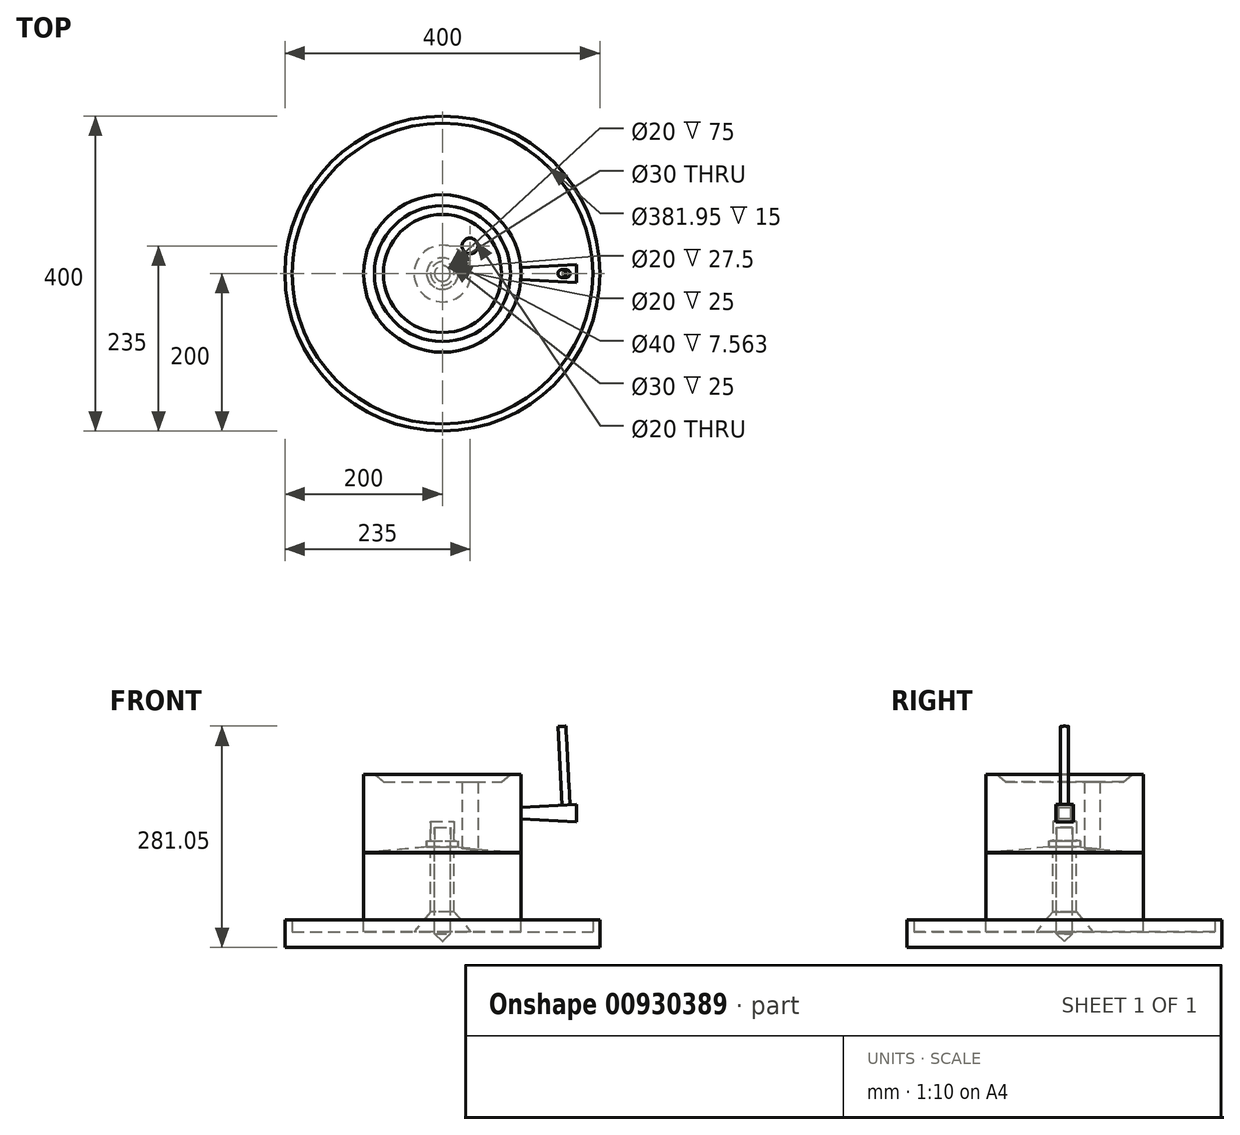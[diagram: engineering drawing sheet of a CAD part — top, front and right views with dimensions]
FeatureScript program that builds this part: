
annotation { "Feature Type Name" : "Feature", "Feature Type Description" : "" }
export const myFeature = defineFeature(function(context is Context, id is Id, definition is map)
    precondition{}
    {
        {
            var Q0;
            Q0=qCreatedBy(makeId("Top.planeOp"),FACE);
            var sketch = newSketch(context, id + "F0", { "sketchPlane" : qUnion([Q0])});
            skCircle(sketch, "E0", {"center": v(0, 0) * mm, "radius": 100 * mm});
            skCircle(sketch, "E1", {"center": v(35, 35) * mm, "radius": 10 * mm});
            skSolve(sketch);
        }
        {
            var Q0;
            Q0 = qSketchRegion(id + "F0", true);
            extrude(context, id + "F1", {"entities" : qUnion([Q0]), "depth" : 100 * mm, "offsetDistance" : 25 * mm});
        }
        {
            var Q0;
            Q0=qCreatedBy(makeId("Front.planeOp"),FACE);
            var sketch = newSketch(context, id + "F2", { "sketchPlane" : qUnion([Q0])});
            skLineSegment(sketch, "E2", {"start": v(0, 40) * mm, "end": v(15, 40) * mm});
            skLineSegment(sketch, "E3", {"start": v(0, 0) * mm, "end": v(0, 40) * mm});
            skLineSegment(sketch, "E4", {"start": v(15, 40) * mm, "end": v(15, 15) * mm});
            skLineSegment(sketch, "E5", {"start": v(15, 15) * mm, "end": v(20, 15) * mm});
            skLineSegment(sketch, "E6", {"start": v(20, 15) * mm, "end": v(20, 0) * mm});
            skLineSegment(sketch, "E7", {"start": v(0, 0) * mm, "end": v(20, 0) * mm});
            skSolve(sketch);
        }
        {
            var Q0;
            Q0 = qSketchRegion(id + "F2", true);
            var Q1;
            Q1=sQuery(id+"F2.wireOp",EDGE,"E3");
            revolve(context, id + "F3", {"operationType" : NewBodyOperationType.REMOVE, "surfaceOperationType" : NewSurfaceOperationType.NEW, "entities" : qUnion([Q0]), "axis" : qUnion([Q1]), "revolveType" : RevolveType.FULL, "oppositeDirection" : true});
        }
        {
            var Q0;
            Q0=qCreatedBy(makeId("Front.planeOp"),FACE);
            var sketch = newSketch(context, id + "F4", { "sketchPlane" : qUnion([Q0])});
            skLineSegment(sketch, "E8", {"start": v(0, 9.19) * mm, "end": v(105, 0) * mm});
            skLineSegment(sketch, "E9", {"start": v(105, 0) * mm, "end": v(0, 0) * mm});
            skLineSegment(sketch, "E10", {"start": v(0, 0) * mm, "end": v(0, 9.19) * mm});
            skSolve(sketch);
        }
        {
            var Q0;
            Q0 = qSketchRegion(id + "F4", true);
            var Q1;
            Q1=sQuery(id+"F4.wireOp",EDGE,"E10");
            revolve(context, id + "F5", {"operationType" : NewBodyOperationType.REMOVE, "surfaceOperationType" : NewSurfaceOperationType.NEW, "entities" : qUnion([Q0]), "axis" : qUnion([Q1]), "revolveType" : RevolveType.FULL, "oppositeDirection" : true});
        }
        {
            var Q0;
            Q0=qCreatedBy(makeId("Top.planeOp"),FACE);
            var sketch = newSketch(context, id + "F6", { "sketchPlane" : qUnion([Q0])});
            skCircle(sketch, "E11", {"center": v(0, 0) * mm, "radius": 100 * mm});
            skSolve(sketch);
        }
        {
            var Q0;
            Q0 = qSketchRegion(id + "F6", true);
            extrude(context, id + "F7", {"entities" : qUnion([Q0]), "oppositeDirection" : true, "depth" : 100 * mm, "offsetDistance" : 25 * mm});
        }
        {
            var Q0;
            Q0=qCreatedBy(makeId("Front.planeOp"),FACE);
            var sketch = newSketch(context, id + "F8", { "sketchPlane" : qUnion([Q0])});
            skLineSegment(sketch, "E12", {"start": v(0, 0) * mm, "end": v(15, 0) * mm});
            skLineSegment(sketch, "E13", {"start": v(15, 0) * mm, "end": v(15, -75) * mm});
            skLineSegment(sketch, "E14", {"start": v(15, -75) * mm, "end": v(35.98, -100) * mm});
            skLineSegment(sketch, "E15", {"start": v(35.98, -100) * mm, "end": v(0, -100) * mm});
            skLineSegment(sketch, "E16", {"start": v(0, -100) * mm, "end": v(0, 0) * mm});
            skSolve(sketch);
        }
        {
            var Q0;
            Q0 = qSketchRegion(id + "F8", true);
            var Q1;
            Q1=sQuery(id+"F8.wireOp",EDGE,"E16");
            revolve(context, id + "F9", {"operationType" : NewBodyOperationType.REMOVE, "surfaceOperationType" : NewSurfaceOperationType.NEW, "entities" : qUnion([Q0]), "axis" : qUnion([Q1]), "revolveType" : RevolveType.FULL, "oppositeDirection" : true});
        }
        {
            var Q0;
            Q0=qCreatedBy(makeId("Front.planeOp"),FACE);
            var sketch = newSketch(context, id + "F10", { "sketchPlane" : qUnion([Q0])});
            skLineSegment(sketch, "E17", {"start": v(0, 90.44) * mm, "end": v(75, 90.44) * mm});
            skLineSegment(sketch, "E18", {"start": v(75, 90.44) * mm, "end": v(86.4, 100) * mm});
            skLineSegment(sketch, "E19", {"start": v(86.4, 100) * mm, "end": v(0, 100) * mm});
            skLineSegment(sketch, "E20", {"start": v(0, 100) * mm, "end": v(0, 90.44) * mm});
            skSolve(sketch);
        }
        {
            var Q0;
            Q0 = qSketchRegion(id + "F10", true);
            var Q1;
            Q1=sQuery(id+"F10.wireOp",EDGE,"E20");
            revolve(context, id + "F11", {"operationType" : NewBodyOperationType.REMOVE, "surfaceOperationType" : NewSurfaceOperationType.NEW, "entities" : qUnion([Q0]), "axis" : qUnion([Q1]), "revolveType" : RevolveType.FULL, "oppositeDirection" : true});
        }
        {
            var Q0;
            Q0=qCreatedBy(makeId("Right.planeOp"),FACE);
            cPlane(context, id + "F12", {"entities" : qUnion([Q0]), "cplaneType" : CPlaneType.OFFSET, "offset" : 100 * mm, "width" : 150 * mm, "height" : 150 * mm});
        }
        {
            var Q0;
            Q0=qCreatedBy(id+"F12.planeOp",FACE);
            var sketch = newSketch(context, id + "F13", { "sketchPlane" : qUnion([Q0])});
            skLineSegment(sketch, "E21.bottom", {"start": v(-7.5, 42.94) * mm, "end": v(7.5, 42.94) * mm});
            skLineSegment(sketch, "E21.top", {"start": v(-7.5, 57.94) * mm, "end": v(7.5, 57.94) * mm});
            skLineSegment(sketch, "E21.left", {"start": v(-7.5, 42.94) * mm, "end": v(-7.5, 57.94) * mm});
            skLineSegment(sketch, "E21.right", {"start": v(7.5, 42.94) * mm, "end": v(7.5, 57.94) * mm});
            skPoint(sketch, "E21.middle", {"position": v(0, 50.44) * mm});
            skSolve(sketch);
        }
        {
            var Q0;
            Q0 = qSketchRegion(id + "F13", true);
            extrude(context, id + "F14", {"entities" : qUnion([Q0]), "operationType" : NewBodyOperationType.REMOVE, "oppositeDirection" : true, "depth" : 30 * mm, "offsetDistance" : 25 * mm, "hasDraft" : true, "draftAngle" : 10 * degree, "draftPullDirection" : true});
        }
        {
            var Q0;
            Q0=makeQuery(id+"F14.boolean.opBoolean","COPY",FACE,{"derivedFrom":makeQuery(id+"F14.opExtrude","CAP_FACE",FACE,{"disambiguationData":[OSD([sQuery(id+"F13.wireOp",EDGE,"E21.bottom"),sQuery(id+"F13.wireOp",EDGE,"E21.top"),sQuery(id+"F13.wireOp",EDGE,"E21.left"),sQuery(id+"F13.wireOp",EDGE,"E21.right")])],"isStart":false})});
            extrude(context, id + "F15", {"entities" : qUnion([Q0]), "depth" : 30 * mm, "offsetDistance" : 25 * mm, "hasDraft" : true, "draftAngle" : 10 * degree});
        }
        {
            var Q0;
            Q0=makeQuery(id+"F13.imprint","IMPRINT",FACE,{"disambiguationData":[TD([[makeQuery(id+"F13.imprint","IMPRINT",EDGE,{"derivedFrom":sQuery(id+"F13.wireOp",EDGE,"E21.bottom")}),1.0]])]});
            extrude(context, id + "F16", {"entities" : qUnion([Q0]), "operationType" : NewBodyOperationType.ADD, "depth" : 70 * mm, "offsetDistance" : 25 * mm, "hasDraft" : true, "draftAngle" : 3 * degree});
        }
        {
            var Q0;
            Q0=makeQuery(id+"F16.opExtrude","SWEPT_FACE",FACE,{"disambiguationData":[OSD([sQuery(id+"F13.wireOp",EDGE,"E21.top")])]});
            var sketch = newSketch(context, id + "F17", { "sketchPlane" : qUnion([Q0])});
            skCircle(sketch, "E22", {"center": v(160, 0) * mm, "radius": 5 * mm});
            skSolve(sketch);
        }
        {
            var Q0;
            Q0 = qSketchRegion(id + "F17", true);
            extrude(context, id + "F18", {"entities" : qUnion([Q0]), "operationType" : NewBodyOperationType.ADD, "depth" : 100 * mm, "offsetDistance" : 25 * mm});
        }
        {
            var Q0;
            Q0=qCreatedBy(makeId("Front.planeOp"),FACE);
            var sketch = newSketch(context, id + "F19", { "sketchPlane" : qUnion([Q0])});
            skLineSegment(sketch, "E23", {"start": v(0, 40) * mm, "end": v(15, 40) * mm});
            skLineSegment(sketch, "E24", {"start": v(15, 40) * mm, "end": v(15, 15) * mm});
            skLineSegment(sketch, "E25", {"start": v(15, 15) * mm, "end": v(20, 15) * mm});
            skLineSegment(sketch, "E26", {"start": v(20, 15) * mm, "end": v(20, 7.5) * mm});
            skLineSegment(sketch, "E27", {"start": v(20, 7.5) * mm, "end": v(0, 7.5) * mm});
            skLineSegment(sketch, "E28", {"start": v(0, 7.5) * mm, "end": v(0, 40) * mm});
            skSolve(sketch);
        }
        {
            var Q0;
            Q0 = qSketchRegion(id + "F19", true);
            var Q1;
            Q1=sQuery(id+"F2.wireOp",EDGE,"E3");
            revolve(context, id + "F20", {"surfaceOperationType" : NewSurfaceOperationType.NEW, "entities" : qUnion([Q0]), "axis" : qUnion([Q1]), "revolveType" : RevolveType.FULL});
        }
        {
            var Q0;
            Q0=makeQuery(id+"F20.opRevolve","SWEPT_FACE",FACE,{"disambiguationData":[OSD([sQuery(id+"F19.wireOp",EDGE,"E27")])]});
            var sketch = newSketch(context, id + "F21", { "sketchPlane" : qUnion([Q0])});
            skCircle(sketch, "E29", {"center": v(0, 0) * mm, "radius": 10 * mm});
            skSolve(sketch);
        }
        {
            var Q0;
            Q0 = qSketchRegion(id + "F21", true);
            extrude(context, id + "F22", {"entities" : qUnion([Q0]), "operationType" : NewBodyOperationType.REMOVE, "oppositeDirection" : true, "depth" : 25 * mm, "offsetDistance" : 25 * mm});
        }
        {
            var Q0;
            Q0=qCreatedBy(makeId("Top.planeOp"),FACE);
            var sketch = newSketch(context, id + "F23", { "sketchPlane" : qUnion([Q0])});
            skCircle(sketch, "E30.0", {"center": v(0, 0) * mm, "radius": 15 * mm});
            skSolve(sketch);
        }
        {
            var Q0;
            Q0 = qSketchRegion(id + "F23", true);
            extrude(context, id + "F24", {"entities" : qUnion([Q0]), "oppositeDirection" : true, "depth" : 75 * mm, "offsetDistance" : 25 * mm});
        }
        {
            var Q0;
            Q0=makeQuery(id+"F24.opExtrude","CAP_FACE",FACE,{"disambiguationData":[OSD([sQuery(id+"F23.wireOp",EDGE,"E30.0")])],"isStart":true});
            var sketch = newSketch(context, id + "F25", { "sketchPlane" : qUnion([Q0])});
            skCircle(sketch, "E31", {"center": v(0, 0) * mm, "radius": 10 * mm});
            skSolve(sketch);
        }
        {
            var Q0;
            Q0 = qSketchRegion(id + "F25", true);
            extrude(context, id + "F26", {"entities" : qUnion([Q0]), "operationType" : NewBodyOperationType.REMOVE, "oppositeDirection" : true, "depth" : 75 * mm, "offsetDistance" : 25 * mm});
        }
        {
            var Q0;
            Q0=makeQuery(id+"F22.boolean.opBoolean","COPY",FACE,{"derivedFrom":makeQuery(id+"F22.opExtrude","CAP_FACE",FACE,{"disambiguationData":[OSD([sQuery(id+"F21.wireOp",EDGE,"E29")])],"isStart":false})});
            var sketch = newSketch(context, id + "F27", { "sketchPlane" : qUnion([Q0])});
            skCircle(sketch, "E32.0.0", {"center": v(0, 0) * mm, "radius": 10 * mm});
            skSolve(sketch);
        }
        {
            var Q0;
            Q0 = qSketchRegion(id + "F27", true);
            extrude(context, id + "F28", {"entities" : qUnion([Q0]), "depth" : 145 * mm, "offsetDistance" : 25 * mm});
        }
        {
            var Q0;
            Q0=makeQuery(id+"F28.opExtrude","CAP_EDGE",EDGE,{"disambiguationData":[OSD([sQuery(id+"F27.wireOp",EDGE,"E32.0.0")])],"isStart":false});
            chamfer(context, id + "F29", {"entities" : qUnion([Q0]), "width" : 10 * mm, "tangentPropagation" : true});
        }
        {
            var Q0;
            Q0=qCreatedBy(makeId("Front.planeOp"),FACE);
            var sketch = newSketch(context, id + "F30", { "sketchPlane" : qUnion([Q0])});
            skLineSegment(sketch, "E33", {"start": v(190.98, -100) * mm, "end": v(190.98, -85) * mm});
            skLineSegment(sketch, "E34", {"start": v(190.98, -85) * mm, "end": v(200, -85) * mm});
            skLineSegment(sketch, "E35", {"start": v(200, -85) * mm, "end": v(200, -120) * mm});
            skLineSegment(sketch, "E36", {"start": v(200, -120) * mm, "end": v(0, -120) * mm});
            skLineSegment(sketch, "E37", {"start": v(0, -120) * mm, "end": v(0, -75) * mm});
            skLineSegment(sketch, "E38", {"start": v(0, -75) * mm, "end": v(15, -75) * mm});
            skLineSegment(sketch, "E39", {"start": v(15, -75) * mm, "end": v(35.98, -100) * mm});
            skLineSegment(sketch, "E40", {"start": v(35.98, -100) * mm, "end": v(190.98, -100) * mm});
            skSolve(sketch);
        }
        {
            var Q0;
            Q0 = qSketchRegion(id + "F30", true);
            var Q1;
            Q1=sQuery(id+"F30.wireOp",EDGE,"E37");
            revolve(context, id + "F31", {"surfaceOperationType" : NewSurfaceOperationType.NEW, "entities" : qUnion([Q0]), "axis" : qUnion([Q1]), "revolveType" : RevolveType.FULL});
        }
        {
            var Q0;
            Q0=makeQuery(id+"F28.opExtrude","SWEPT_BODY",BODY,{"disambiguationData":[OSD([sQuery(id+"F27.wireOp",EDGE,"E32.0.0")])]});
            var Q1;
            Q1=makeQuery(id+"F31.opRevolve","SWEPT_BODY",BODY,{"disambiguationData":[OSD([sQuery(id+"F30.wireOp",EDGE,"x0PHMXUQ-w0mN-wSCU-o6u4-OQjVglI4lZyS"),sQuery(id+"F30.wireOp",EDGE,"E33"),sQuery(id+"F30.wireOp",EDGE,"E34"),sQuery(id+"F30.wireOp",EDGE,"E35"),sQuery(id+"F30.wireOp",EDGE,"E36"),sQuery(id+"F30.wireOp",EDGE,"h7mgvtze-5PXb-mjpW-W06Y-tg9THzuJcQCp")])]});
            booleanBodies(context, id + "F32", {"operationType" : BooleanOperationType.SUBTRACTION, "tools" : qUnion([Q0]), "targets" : qUnion([Q1]), "keepTools" : true});
        }
    });
